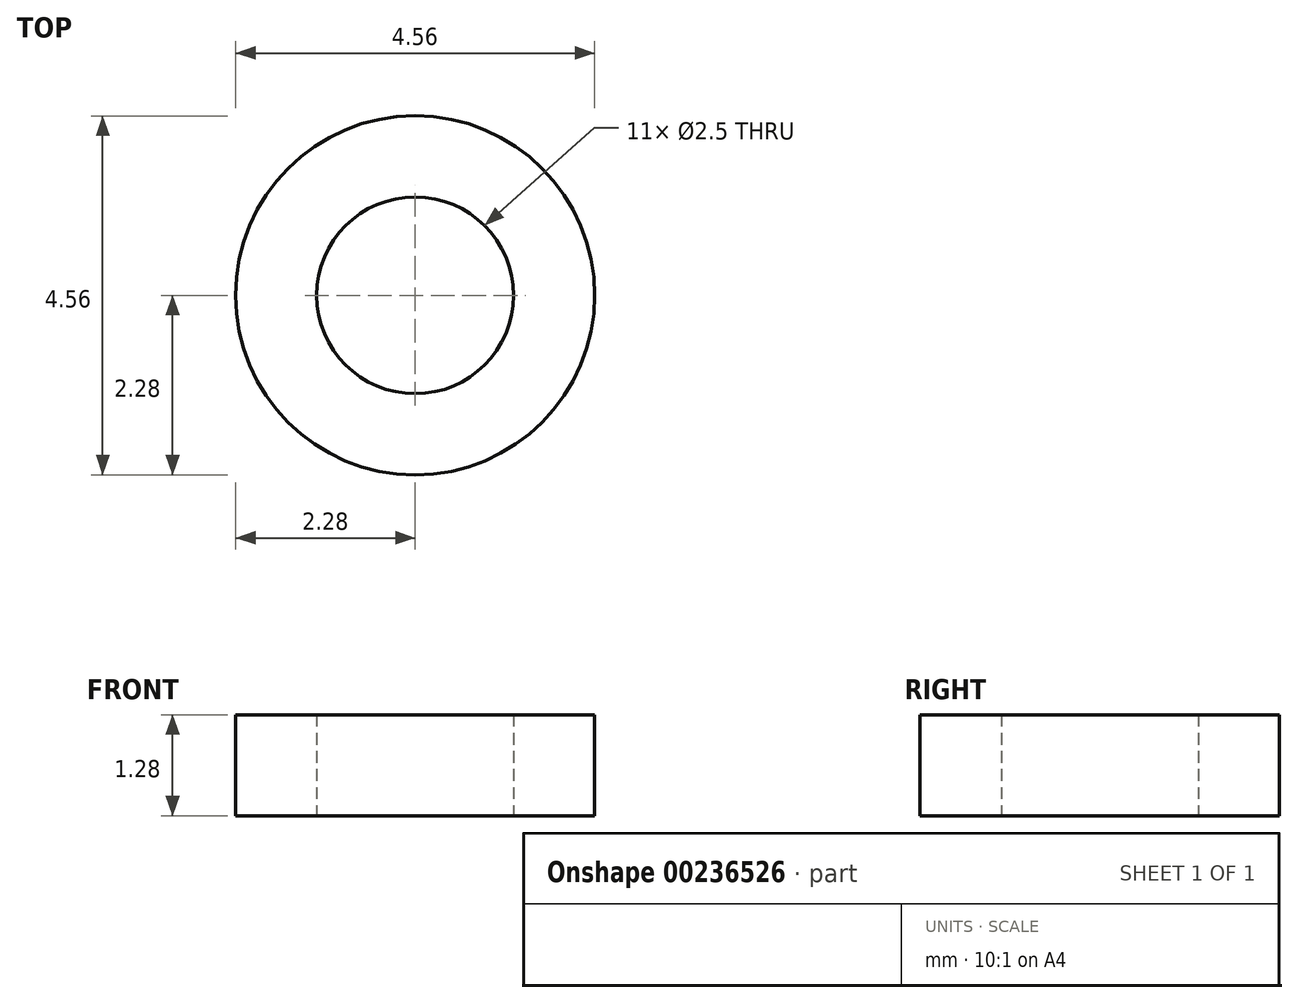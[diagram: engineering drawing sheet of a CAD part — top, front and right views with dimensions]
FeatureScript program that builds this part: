
annotation { "Feature Type Name" : "Feature", "Feature Type Description" : "" }
export const myFeature = defineFeature(function(context is Context, id is Id, definition is map)
    precondition{}
    {
        {
            assignVariable(context, id + "F0", {"name" : "scale", "anyValue" : 1 / 160});
        }
        {
            var Q0;
            Q0=qCreatedBy(makeId("Top.planeOp"),FACE);
            var sketch = newSketch(context, id + "F1", { "sketchPlane" : qUnion([Q0])});
            skCircle(sketch, "E0", {"center": v(0, 0) * mm, "radius": 2.28 * mm});
            skCircle(sketch, "E1", {"center": v(0, 0) * mm, "radius": 1.25 * mm});
            skSolve(sketch);
        }
        {
            var Q0;
            Q0=qSketchRegion(id+"F1",true);
            extrude(context, id + "F2", {"entities" : qUnion([Q0]), "depth" : 205 * getVariable(context, 'scale') * mm});
        }
    });
